# Revit family: 93710103
name_source: partatom
category: Modelos genéricos
revit_build: Autodesk Revit 2016 (Build: 20150220_1215(x64)
units: mm (PartAtom-declared; Revit-internal decimal feet)

## family parameters
Com base no plano de trabalho = Não
Compartilhado = Não
Corte com vazios quando carregados = Não
Cota do conector redondo = Utilizar diâmetro
Pode hospedar o vergalhão = Não
Ponto de cálculo do ambiente = Não
Sempre na vertical = Sim
Tipo de parte = Normal

## types (2) — shared parameters
Categoria = II 2, 3
Comentários de tipos = Ler Manual de Instalação
Código de montagem = 93710-103
Dados de instalação = http://www.tramontina.com.br
Descrição = 93710-103
Desenvolvedor = Factory Cursos & Desenvolvimento
Diametro = 48  [stored 0.15748 ft]
Dimensões (mm) = 1200 x 550
Fabricante = Tramontina
Modelo = Tramontina Pia Fogão - 93710-103
Peso bruto = 11,8
Peso líquido = 8,6 kg
Potência Elétrica = 3 W
Queimador auxiliar (kW) = 1  [stored 0.00328084 ft]
Queimador rápido (kW) = 2  [stored 0.00656168 ft]
Site do desenvolvedor = www.factorycursos.com.br
Sum Qn (kW) = 3  [stored 0.00984252 ft]
Tipo de gás - G20 Natural = 1,96 kPa (20 mbar)
Tipo de gás - G30 (butano) = 2,75 kPa (28- 32 mbar)
Tipo de imagem = 93710-103 - PIA FOGAO STAR 40 2GX_DESENHO.jpg
URL = www.tramontina.com.br

## per-type parameters (varying)
| type | Frequência | Tensão |
| Tramontina Pia-Fogão - 93710-103 (127 Volts) | 50 HZ | 127 V |
| Tramontina Pia-Fogão - 93710-103 (220 Volts) | 60 HZ | 220 V |

note: [stored X ft] marks values corroborated as IEEE doubles in the binary element streams (Revit-internal decimal feet)
